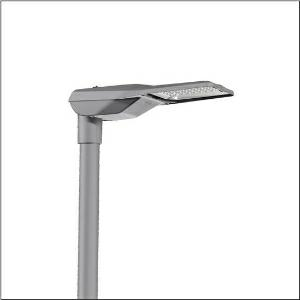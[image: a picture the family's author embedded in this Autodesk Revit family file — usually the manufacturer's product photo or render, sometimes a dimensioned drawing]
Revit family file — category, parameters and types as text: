
# Revit family: streetlight_sl_21_mini___p1_0a_5xe2a43s08hb_0f60
name_source: partatom
category: Lighting Fixtures
units: mm (PartAtom-declared; Revit-internal decimal feet)

## family parameters
Cut with Voids When Loaded = No
Host = Face
Light Source = No
Part Type = Normal
Room Calculation Point = No
Round Connector Dimension = Use Diameter
Shared = No

## types (1)
- --- (1 x LED, 9430 lm, 66 W, 4000K)
    Apparent Load = 66 VA
    CIE Flux Codes = 21 50 90 100 100
    Color Rendering = 70
    Color Temperature = 4000K
    Default Elevation = 1800 mm
    Description = Streetlight SL 21 mini, mast luminaire, primary light control with lens, of PMMA, primary optical cover: cover, of toughened safety glass, transparent, light distribution: P1.0a, light emission: direct distribution, primary light characteristic: asymmetric, installation type: side-entry, post-top, LED, High Power LED, rated luminous flux: 9.430lm, luminous efficacy: 143lm/W, light colour: 740, colour temperature: 4000K, control gear: D4i, control: overheat protection, constant luminous flux control, time-dependent luminous flux control, flexible luminous flux parameterisation, pre-setting: logarithmic dimming characteristic, mains connection: 220..240V, AC, 50/60Hz, start of lifetime: 66W, end of service life: 69W, reduction: 30W, luminaire housing, of diecast aluminium, powder-coated, SITECO metallic grey (DB 702S), corrosivity category C5 high according to DIN EN ISO 12944, please order mast flange separately, inclination adjustable: 0°, 5°, 10°, 15°, sealing non-destructively replaceable, multi-level sealing system, length: 628mm, width: 235mm, height: 110mm, mast flange for spigot size: 42mm (side-entry): 5XC10008XM4, 60/48mm (side-entry/post-top): 5XC10108XM2, 76/60mm (side-entry/post-top): 5XC10108XM1, mounting height: 4..8m, Smart Interface above, protection rating (complete): IP66, insulation class (complete): insulation class II (safety insulation), certification: CE, ENEC, ENEC+, VDE, impact resistance: IK10, permissible operating ambient temperature for outdoor applications: -40..+50°C, standard-compliant lighting for roads and squares, packaging unit: 1 piece

Light Distribution: P1.0a
    Height = 110 mm
    Lamp = 1 x LED
    Lamp Light Flux = 9430 lm
    Lamp Power = 66 W
    Lamp count = 1
    Length = 625 mm
    Luminous efficacy = 143 lm/W
    Manufacturer = Siteco
    ModVariant = No
    Model = 5XE2A43S08HB
    Number of Poles = 1
    OnlyDefault = Yes
    Power Factor = 1
    Product Name = Streetlight SL 21 mini | P1.0a
    Product group = mast luminaire | pylon top
    ProductGroupID = 6100
    Protection Class = Protection class II
    Protection Degree = IP 66
    RLX_Detail_Level = 1
    RLX_Emergency_Light_Flux = 0 lm
    RLX_Emergency_Type = 0
    RLX_Emergency_Type_DB = No
    RlxData = <blob elided: 37349 chars, md5=1cc18e6c>
    Socket = socket
    Standby Power = 0 W
    System Light Flux = 9430 lm
    System Power = 66 W
    Type Comments = factory setting: luminous flux: 100 % | dim-lin: 254 | 670 mA
    Type Image = l_1003515.jpg
    URL = http://relux.com
    VarID = @adj_184055
    Voltage = 0 V
    Weight = 0.00 kg
    Width = 234 mm

## geometry (parser evidence)
native form markers: Blend x4, Sweep x12
no freeform markers — native parametric forms only
